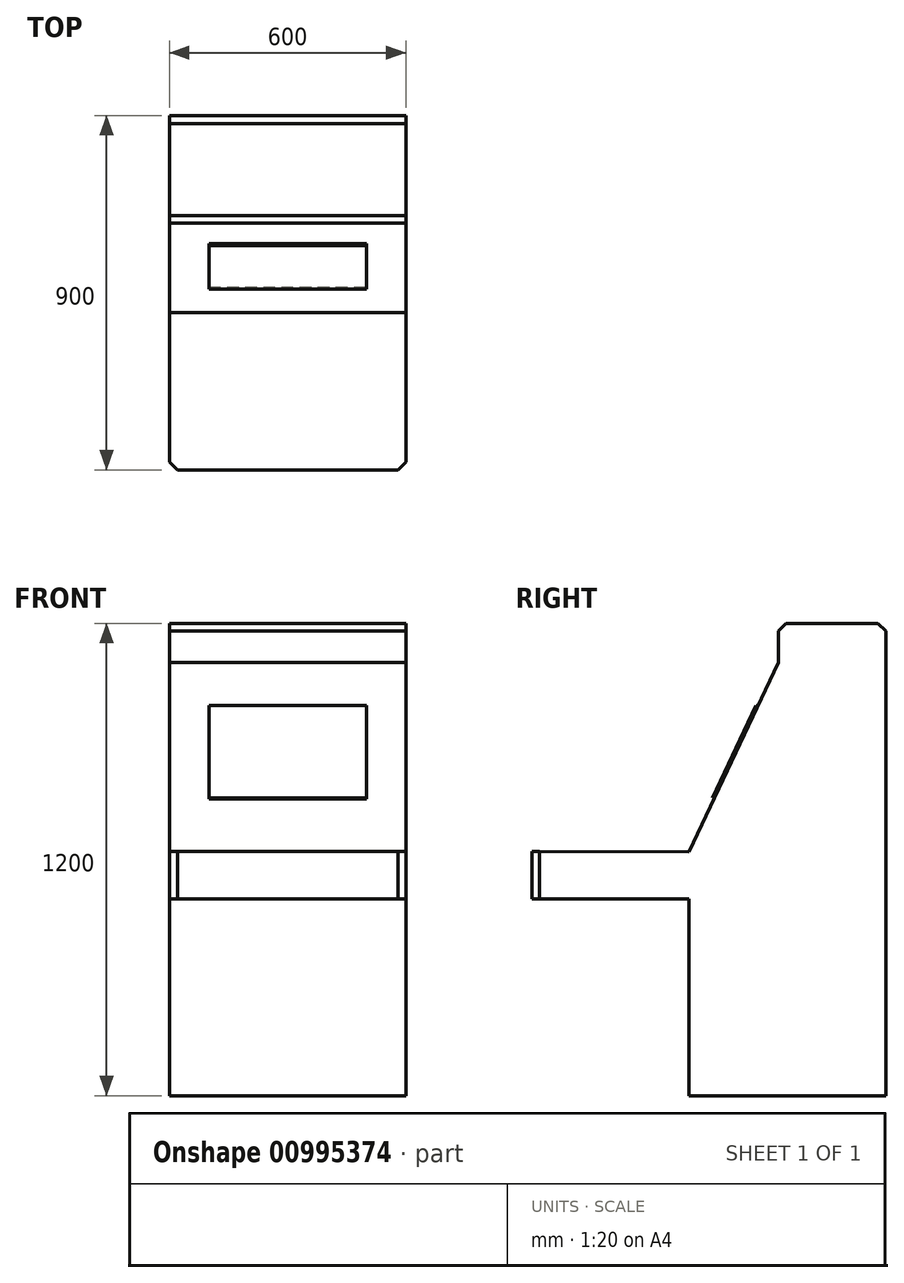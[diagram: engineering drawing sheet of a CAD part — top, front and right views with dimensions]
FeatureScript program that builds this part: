
annotation { "Feature Type Name" : "Feature", "Feature Type Description" : "" }
export const myFeature = defineFeature(function(context is Context, id is Id, definition is map)
    precondition{}
    {
        {
            var Q0;
            Q0=qCreatedBy(makeId("Right.planeOp"),FACE);
            var sketch = newSketch(context, id + "F0", { "sketchPlane" : qUnion([Q0])});
            skLineSegment(sketch, "E0", {"start": v(275.5, 657.85) * mm, "end": v(549.16, 657.85) * mm});
            skLineSegment(sketch, "E1", {"start": v(549.16, 657.85) * mm, "end": v(549.16, -542.15) * mm});
            skLineSegment(sketch, "E2", {"start": v(549.16, -542.15) * mm, "end": v(49.16, -542.15) * mm});
            skLineSegment(sketch, "E3", {"start": v(49.16, -542.15) * mm, "end": v(49.16, -42.15) * mm});
            skLineSegment(sketch, "E4", {"start": v(49.16, -42.15) * mm, "end": v(-350.84, -42.15) * mm});
            skLineSegment(sketch, "E5", {"start": v(-350.84, -42.15) * mm, "end": v(-350.84, 77.85) * mm});
            skLineSegment(sketch, "E6", {"start": v(-350.84, 77.85) * mm, "end": v(49.16, 76.55) * mm});
            skLineSegment(sketch, "E7", {"start": v(49.16, 76.55) * mm, "end": v(275.5, 557.85) * mm});
            skLineSegment(sketch, "E8", {"start": v(275.5, 557.85) * mm, "end": v(275.5, 657.85) * mm});
            skSolve(sketch);
        }
        {
            var Q0;
            Q0=makeQuery(id+"F0.imprint","IMPRINT",FACE,{"disambiguationData":[TD([[makeQuery(id+"F0.imprint","IMPRINT",EDGE,{"derivedFrom":sQuery(id+"F0.wireOp",EDGE,"E0")}),-1.0]])]});
            extrude(context, id + "F1", {"entities" : qUnion([Q0]), "depth" : 600 * mm, "offsetDistance" : 25 * mm});
        }
        {
            var Q0;
            Q0=makeQuery(id+"F1.opExtrude","SWEPT_FACE",FACE,{"disambiguationData":[OSD([sQuery(id+"F0.wireOp",EDGE,"E7")])]});
            var sketch = newSketch(context, id + "F2", { "sketchPlane" : qUnion([Q0])});
            skLineSegment(sketch, "E9.bottom", {"start": v(100, 500.2) * mm, "end": v(500, 500.2) * mm});
            skLineSegment(sketch, "E9.top", {"start": v(100, 240.2) * mm, "end": v(500, 240.2) * mm});
            skLineSegment(sketch, "E9.left", {"start": v(100, 500.2) * mm, "end": v(100, 240.2) * mm});
            skLineSegment(sketch, "E9.right", {"start": v(500, 500.2) * mm, "end": v(500, 240.2) * mm});
            skSolve(sketch);
        }
        {
            var Q0;
            Q0=makeQuery(id+"F2.imprint","IMPRINT",FACE,{"disambiguationData":[TD([[makeQuery(id+"F2.imprint","IMPRINT",EDGE,{"derivedFrom":sQuery(id+"F2.wireOp",EDGE,"E9.bottom")}),-1.0]])]});
            extrude(context, id + "F3", {"entities" : qUnion([Q0]), "operationType" : NewBodyOperationType.ADD, "depth" : 5 * mm, "offsetDistance" : 25 * mm});
        }
        {
            var Q0;
            Q0=makeQuery(id+"F1.opExtrude","SWEPT_EDGE",EDGE,{"disambiguationData":[OSD([sQuery(id+"F0.wireOp",EDGE,"E0"),sQuery(id+"F0.wireOp",EDGE,"E8")])]});
            var Q1;
            Q1=makeQuery(id+"F1.opExtrude","SWEPT_EDGE",EDGE,{"disambiguationData":[OSD([sQuery(id+"F0.wireOp",EDGE,"E0"),sQuery(id+"F0.wireOp",EDGE,"E1")])]});
            var Q2;
            Q2=makeQuery(id+"F1.opExtrude","CAP_EDGE",EDGE,{"disambiguationData":[OSD([sQuery(id+"F0.wireOp",EDGE,"E5")])],"isStart":false});
            var Q3;
            Q3=makeQuery(id+"F1.opExtrude","CAP_EDGE",EDGE,{"disambiguationData":[OSD([sQuery(id+"F0.wireOp",EDGE,"E5")])],"isStart":true});
            chamfer(context, id + "F4", {"entities" : qUnion([Q0, Q1, Q2, Q3]), "width" : 20 * mm, "tangentPropagation" : true});
        }
    });
